annotation { "Feature Type Name" : "Feature", "Feature Type Description" : "" }
export const myFeature = defineFeature(function(context is Context, id is Id, definition is map)
    precondition{}
    {
        {
            var Q0;
            Q0=qCreatedBy(makeId("Front.planeOp"),FACE);
            var sketch = newSketch(context, id + "F0", { "sketchPlane" : qUnion([Q0])});
            skLineSegment(sketch, "E0.bottom", {"start": v(-7.5, 4) * mm, "end": v(7.5, 4) * mm});
            skLineSegment(sketch, "E0.top", {"start": v(-7.5, -4) * mm, "end": v(7.5, -4) * mm});
            skLineSegment(sketch, "E0.left", {"start": v(-8.5, 3) * mm, "end": v(-8.5, -3) * mm});
            skLineSegment(sketch, "E0.right", {"start": v(8.5, 3) * mm, "end": v(8.5, -3) * mm});
            skPoint(sketch, "E1.visualSharp", {"position": v(-8.5, 4) * mm});
            skArc(sketch, "E1.filletArc", {"start": v(-7.9, 3.91) * mm, "mid": v(-8.34, 3.55) * mm, "end": v(-8.5, 3) * mm});
            skPoint(sketch, "E2.visualSharp", {"position": v(-8.5, -4) * mm});
            skArc(sketch, "E2.filletArc", {"start": v(-8.5, -3) * mm, "mid": v(-8.2, -3.7) * mm, "end": v(-7.5, -4) * mm});
            skPoint(sketch, "E3.visualSharp", {"position": v(8.5, 4) * mm});
            skArc(sketch, "E3.filletArc", {"start": v(8.5, 3) * mm, "mid": v(8.2, 3.7) * mm, "end": v(7.5, 4) * mm});
            skPoint(sketch, "E4.visualSharp", {"position": v(8.5, -4) * mm});
            skArc(sketch, "E4.filletArc", {"start": v(7.5, -4) * mm, "mid": v(8.2, -3.7) * mm, "end": v(8.5, -3) * mm});
            skPoint(sketch, "E5.visualSharp", {"position": v(-7.5, 4) * mm});
            skArc(sketch, "E5.filletArc", {"start": v(-7.5, 4) * mm, "mid": v(-7.7, 3.98) * mm, "end": v(-7.9, 3.91) * mm});
            skSolve(sketch);
        }
        {
            var Q0;
            Q0 = qSketchRegion(id + "F0", true);
            var Q1;
            Q1 = qSketchRegion(id + "FKFxGJkvdqiMW3Z_1", true);
            extrude(context, id + "F1", {"entities" : qUnion([Q0, Q1]), "depth" : 55 * mm, "offsetDistance" : 25 * mm});
        }
        {
            var Q0;
            Q0=makeQuery(id+"F1.opExtrude","CAP_FACE",FACE,{"disambiguationData":[OSD([sQuery(id+"F0.wireOp",EDGE,"E0.bottom"),sQuery(id+"F0.wireOp",EDGE,"E0.top"),sQuery(id+"F0.wireOp",EDGE,"E0.left"),sQuery(id+"F0.wireOp",EDGE,"E0.right"),sQuery(id+"F0.wireOp",EDGE,"E1.filletArc"),sQuery(id+"F0.wireOp",EDGE,"E2.filletArc"),sQuery(id+"F0.wireOp",EDGE,"E3.filletArc"),sQuery(id+"F0.wireOp",EDGE,"E4.filletArc"),sQuery(id+"F0.wireOp",EDGE,"E5.filletArc")])],"isStart":false});
            var sketch = newSketch(context, id + "F2", { "sketchPlane" : qUnion([Q0])});
            skLineSegment(sketch, "E6.bottom", {"start": v(-6.2, 2.5) * mm, "end": v(6.2, 2.5) * mm});
            skLineSegment(sketch, "E6.top", {"start": v(-6.2, -2.5) * mm, "end": v(6.2, -2.5) * mm});
            skLineSegment(sketch, "E6.left", {"start": v(-6.2, 2.5) * mm, "end": v(-6.2, -2.5) * mm});
            skLineSegment(sketch, "E6.right", {"start": v(6.2, 2.5) * mm, "end": v(6.2, -2.5) * mm});
            skSolve(sketch);
        }
        {
            var Q0;
            Q0 = qSketchRegion(id + "F2", true);
            extrude(context, id + "F3", {"entities" : qUnion([Q0]), "operationType" : NewBodyOperationType.REMOVE, "oppositeDirection" : true, "depth" : 14 * mm, "offsetDistance" : 25 * mm});
        }
        {
            var Q0;
            Q0=makeQuery(id+"F1.opExtrude","SWEPT_BODY",BODY,{"disambiguationData":[OSD([sQuery(id+"F0.wireOp",EDGE,"E0.bottom"),sQuery(id+"F0.wireOp",EDGE,"E0.top"),sQuery(id+"F0.wireOp",EDGE,"E0.left"),sQuery(id+"F0.wireOp",EDGE,"E0.right"),sQuery(id+"F0.wireOp",EDGE,"E1.filletArc"),sQuery(id+"F0.wireOp",EDGE,"E2.filletArc"),sQuery(id+"F0.wireOp",EDGE,"E3.filletArc"),sQuery(id+"F0.wireOp",EDGE,"E4.filletArc"),sQuery(id+"F0.wireOp",EDGE,"E5.filletArc")])]});
            var Q1;
            Q1=makeQuery(id+"F1.opExtrude","CAP_EDGE",EDGE,{"disambiguationData":[OSD([sQuery(id+"F0.wireOp",EDGE,"E0.right")])],"isStart":true});
            transform(context, id + "F4", {"entities" : qUnion([Q0]), "transformType" : TransformType.ROTATION, "transformAxis" : qUnion([Q1]), "angle" : 90 * degree, "makeCopy" : false});
        }
        {
            var Q0;
            Q0=makeQuery(id+"F1.opExtrude","SWEPT_FACE",FACE,{"disambiguationData":[OSD([sQuery(id+"F0.wireOp",EDGE,"E0.bottom")])]});
            var sketch = newSketch(context, id + "F5", { "sketchPlane" : qUnion([Q0])});
            skText(sketch, "E7", { "text": "SHAD UBC 2017", "fontName": "AllertaStencil-Regular.ttf"});
            const initialGuessF5  = {"E7": [-0.04553, 0.00962, 1, 0, 0.005]};
            skSetInitialGuess(sketch, initialGuessF5);
            skSolve(sketch);
        }
        {
            var Q0;
            Q0=makeQuery(id+"F5.imprint","IMPRINT",FACE,{"disambiguationData":[TD([[makeQuery(id+"F5.imprint","IMPRINT",EDGE,{"derivedFrom":sQuery(id+"F5.wireOp",EDGE,"E7.sketch_text.stroke-0")}),1.0]])]});
            var sketch = newSketch(context, id + "F6", { "sketchPlane" : qUnion([Q0])});
            skText(sketch, "E8", { "text": "Lucia Wang", "fontName": "AllertaStencil-Regular.ttf"});
            const initialGuessF6  = {"E8": [-0.03824, 0.00321, 1, 0, 0.005]};
            skSetInitialGuess(sketch, initialGuessF6);
            skSolve(sketch);
        }
        {
            var Q0;
            Q0 = qSketchRegion(id + "F5", true);
            extrude(context, id + "F7", {"entities" : qUnion([Q0]), "operationType" : NewBodyOperationType.REMOVE, "oppositeDirection" : true, "depth" : 10 * mm, "offsetDistance" : 25 * mm});
        }
        {
            var Q0;
            Q0 = qSketchRegion(id + "F6", true);
            extrude(context, id + "F8", {"entities" : qUnion([Q0]), "operationType" : NewBodyOperationType.REMOVE, "oppositeDirection" : true, "depth" : 10 * mm, "offsetDistance" : 25 * mm});
        }
    });